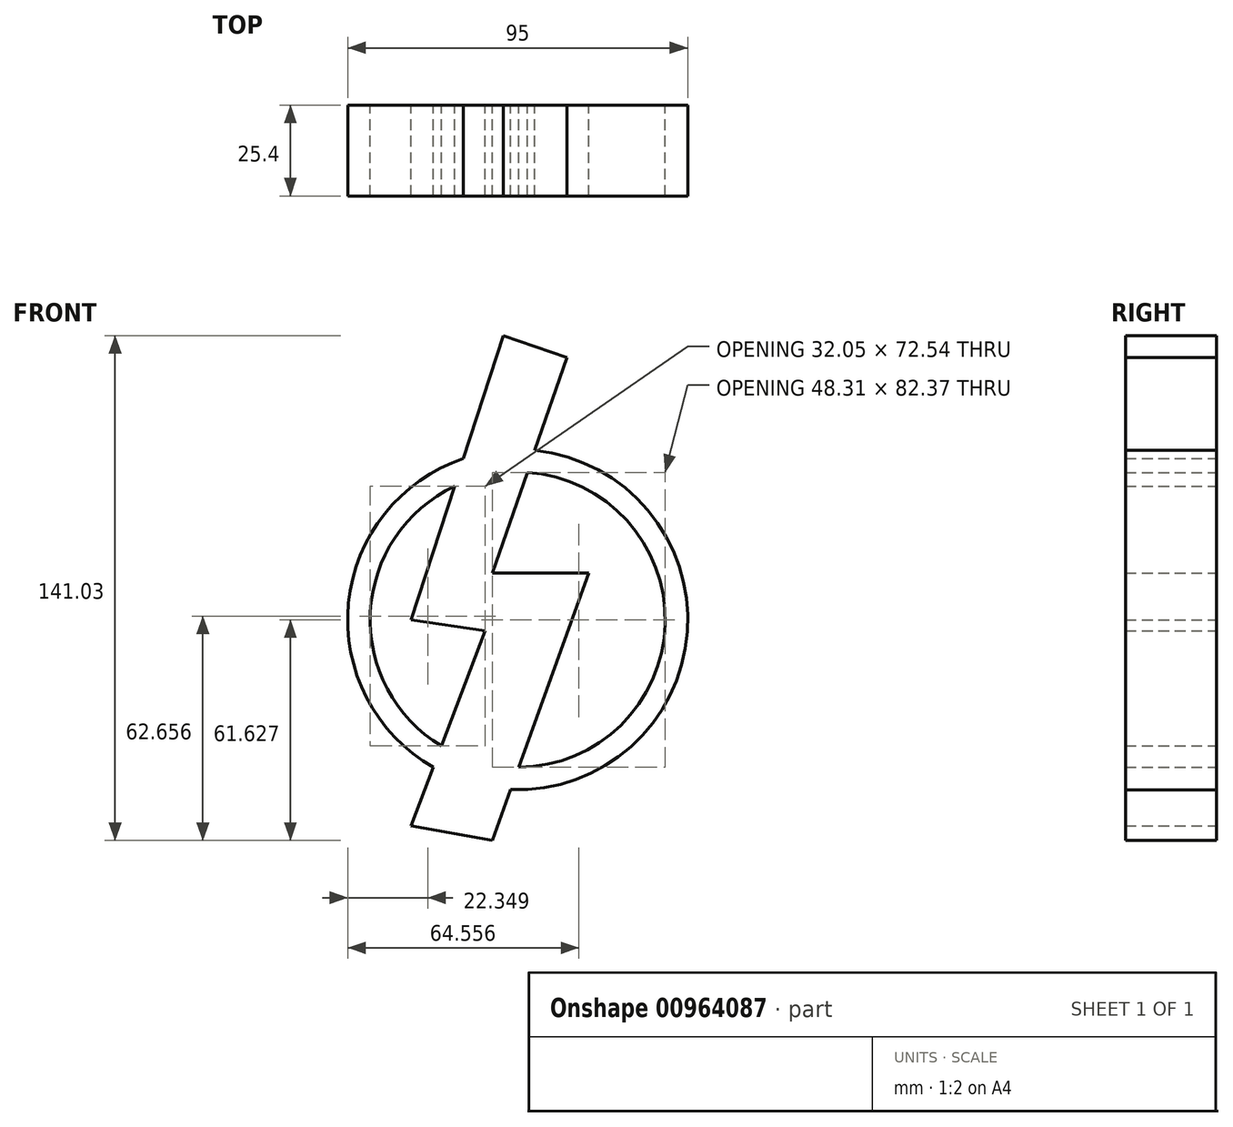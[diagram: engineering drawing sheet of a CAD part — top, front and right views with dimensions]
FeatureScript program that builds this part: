
annotation { "Feature Type Name" : "Feature", "Feature Type Description" : "" }
export const myFeature = defineFeature(function(context is Context, id is Id, definition is map)
    precondition{}
    {
        {
            var Q0;
            Q0=qCreatedBy(makeId("Front.planeOp"),FACE);
            var sketch = newSketch(context, id + "F0", { "sketchPlane" : qUnion([Q0])});
            skCircle(sketch, "E0", {"center": v(0, 0) * mm, "radius": 47.5 * mm});
            skCircle(sketch, "E1", {"center": v(0, 0) * mm, "radius": 41.23 * mm});
            skSolve(sketch);
        }
        {
            var Q0;
            Q0=makeQuery(id+"F0.imprint","IMPRINT",FACE,{"disambiguationData":[TD([[makeQuery(id+"F0.imprint","IMPRINT",EDGE,{"derivedFrom":sQuery(id+"F0.wireOp",EDGE,"E0")}),1.0]])]});
            extrude(context, id + "F1", {"entities" : qUnion([Q0]), "depth" : 25.4 * mm, "offsetDistance" : 25.4 * mm});
        }
        {
            var Q0;
            Q0=qCreatedBy(makeId("Front.planeOp"),FACE);
            var sketch = newSketch(context, id + "F2", { "sketchPlane" : qUnion([Q0])});
            skLineSegment(sketch, "E2", {"start": v(13.8, 73.2) * mm, "end": v(-7.1, 13) * mm});
            skLineSegment(sketch, "E3", {"start": v(-7.1, 13) * mm, "end": v(19.82, 13) * mm});
            skLineSegment(sketch, "E4", {"start": v(19.82, 13) * mm, "end": v(-7.1, -61.67) * mm});
            skLineSegment(sketch, "E5", {"start": v(13.8, 73.2) * mm, "end": v(-3.96, 79.36) * mm});
            skLineSegment(sketch, "E6", {"start": v(-3.96, 79.36) * mm, "end": v(-29.77, 0) * mm});
            skLineSegment(sketch, "E7", {"start": v(-29.77, 0) * mm, "end": v(-9.13, -3.04) * mm});
            skLineSegment(sketch, "E8", {"start": v(-9.13, -3.04) * mm, "end": v(-29.77, -57.61) * mm});
            skLineSegment(sketch, "E9", {"start": v(-29.77, -57.61) * mm, "end": v(-7.1, -61.67) * mm});
            skSolve(sketch);
        }
        {
            var Q0;
            Q0 = qSketchRegion(id + "F2", true);
            extrude(context, id + "F3", {"entities" : qUnion([Q0]), "operationType" : NewBodyOperationType.ADD, "depth" : 25.4 * mm, "offsetDistance" : 25.4 * mm});
        }
    });
